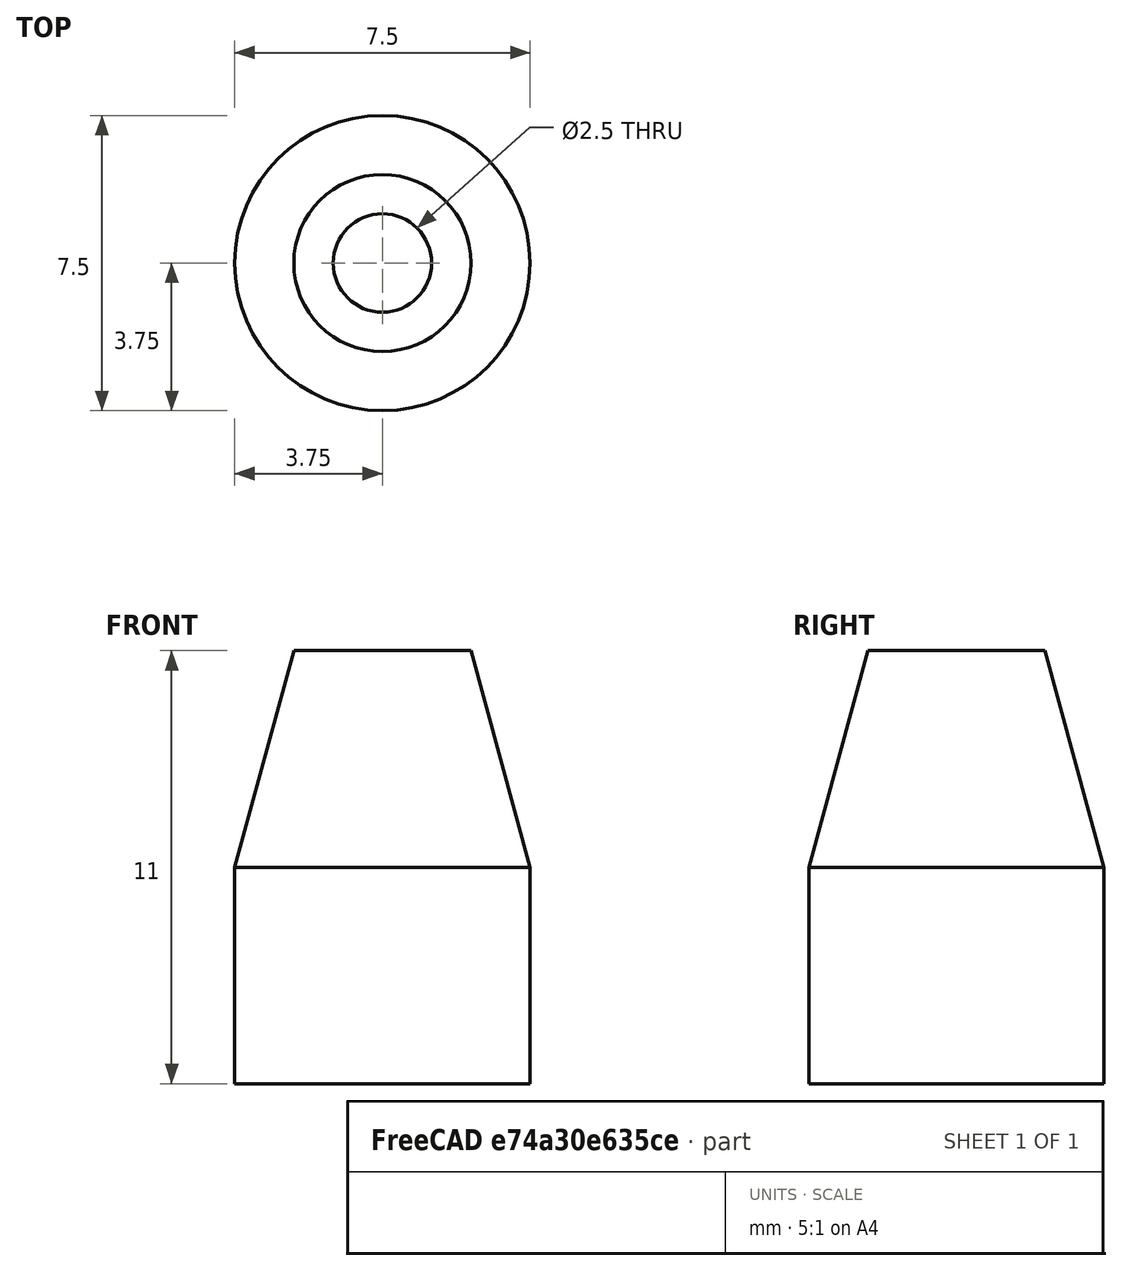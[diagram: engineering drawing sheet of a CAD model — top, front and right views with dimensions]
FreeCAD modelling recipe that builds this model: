
FCSTD DOCUMENT  (FreeCAD 0.19R)
Label: x-axis-camera-spacer
License: All rights reserved
LicenseURL: http://en.wikipedia.org/wiki/All_rights_reserved
objects: Sketcher::SketchObject×1, PartDesign::Revolution×1, PartDesign::Body×1
note: 4 computed .brp shape members not serialized (recipe doc carries the construction recipe); baked Part::Feature solids carry a one-line shape summary decoded from their .brp

FEATURE [Sketcher::SketchObject] Sketch
  FullyConstrained = true
  MapMode = 5
  Placement = pos=(0,0,0) rot=(1,0,0;1.5708rad)
  Support = -> [XZ_Plane]
  sketch-geometry (5):
    g0: LineSegment StartX=1.25 StartY=0 StartZ=0 EndX=1.25 EndY=11 EndZ=0
    g1: LineSegment StartX=1.25 StartY=11 StartZ=0 EndX=2.25 EndY=11 EndZ=0
    g2: LineSegment StartX=2.25 StartY=11 StartZ=0 EndX=3.75 EndY=5.5 EndZ=0
    g3: LineSegment StartX=3.75 StartY=5.5 StartZ=0 EndX=3.75 EndY=0 EndZ=0
    g4: LineSegment StartX=3.75 StartY=0 StartZ=0 EndX=1.25 EndY=0 EndZ=0
  constraints (15):
    c: PointOnObject(g0,g-1)
    c: Vertical(g0)
    c: Coincident(g1,g0)
    c: Horizontal(g1)
    c: Coincident(g2,g1)
    c: Coincident(g3,g2)
    c: PointOnObject(g3,g-1)
    c: Vertical(g3)
    c: Coincident(g4,g3)
    c: Coincident(g4,g0)
    c: DistanceY(g3,g3) = 5.5
    c: DistanceY(g0,g0) = 11
    c: DistanceX(g-1,g0) = 1.25
    c: DistanceX(g4,g4) = 2.5
    c: DistanceX(g1,g1) = 1
FEATURE [PartDesign::Revolution] Revolution
  Angle = 360
  Axis = (0,-2e-16,1)
  Base = (0,0,0)
  Placement = pos=(0,0,0) rot=(1,0,0;1.5708rad)
  Profile = -> Sketch
  ReferenceAxis = -> Sketch [V_Axis]
  Reversed = true
FEATURE [PartDesign::Body] Body
  Group = -> [Sketch,Revolution]
  Origin = -> Origin
  Tip = -> Revolution
